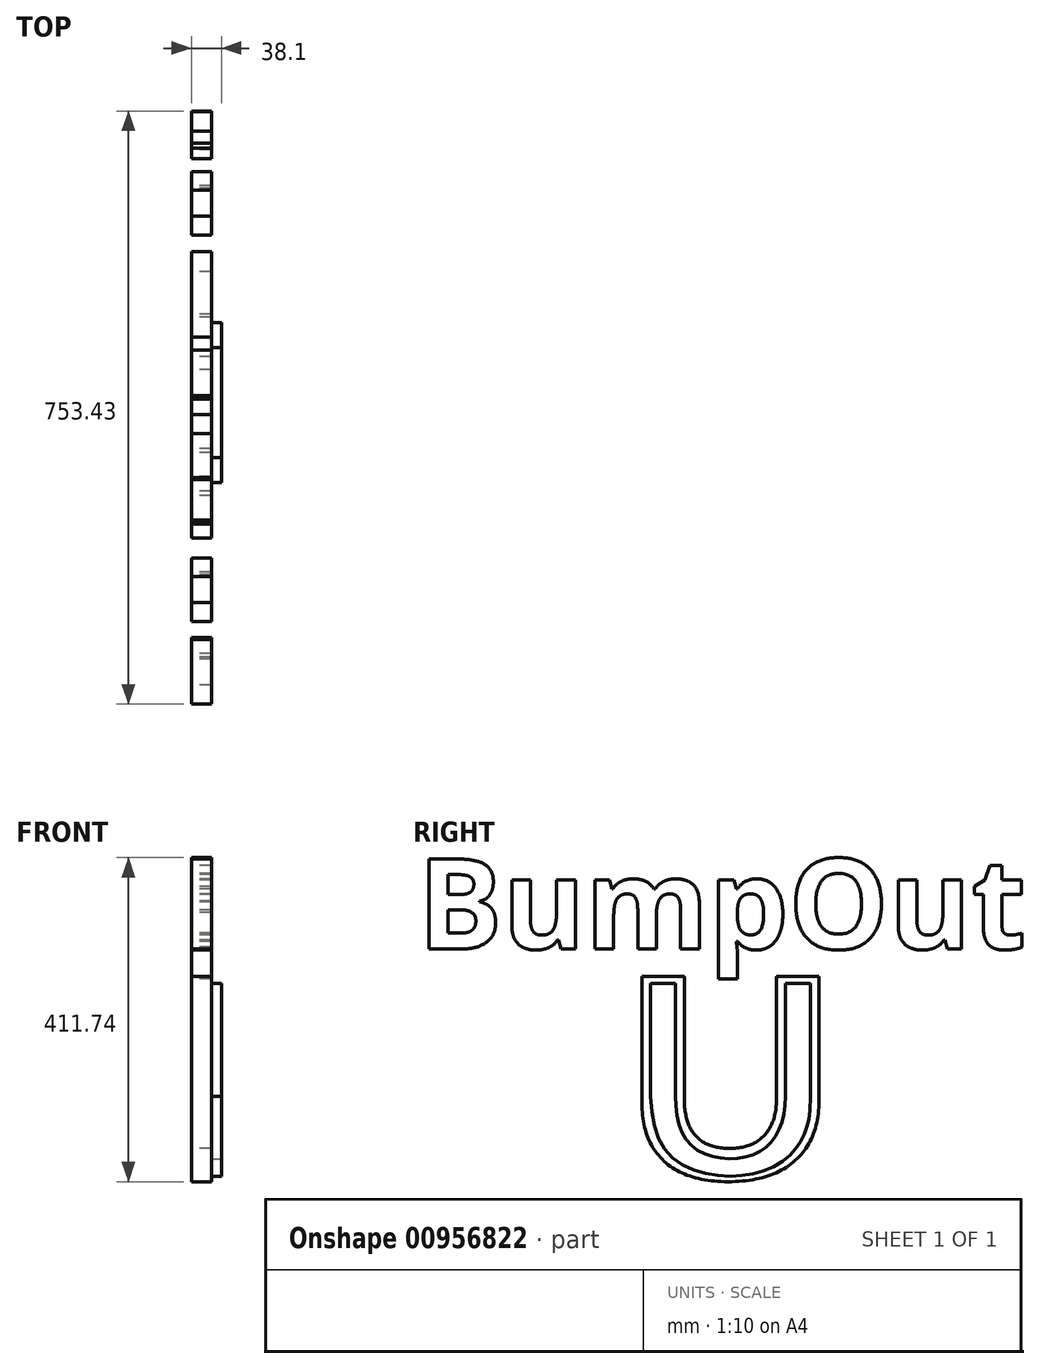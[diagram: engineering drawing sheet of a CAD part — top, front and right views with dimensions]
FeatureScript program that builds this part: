
annotation { "Feature Type Name" : "Feature", "Feature Type Description" : "" }
export const myFeature = defineFeature(function(context is Context, id is Id, definition is map)
    precondition{}
    {
        {
            var Q0;
            Q0=qCreatedBy(makeId("Right.planeOp"),FACE);
            var sketch = newSketch(context, id + "F0", { "sketchPlane" : qUnion([Q0])});
            skText(sketch, "E0", { "text": "BumpOut", "fontName": "OpenSans-Bold.ttf"});
            const initialGuessF0  = {"E0": [-0.07763, -0.0437, 1, 0, 0.1152]};
            skSetInitialGuess(sketch, initialGuessF0);
            skSolve(sketch);
        }
        {
            var Q0;
            Q0=makeQuery(id+"F0.imprint","IMPRINT",FACE,{"disambiguationData":[TD([[makeQuery(id+"F0.imprint","IMPRINT",EDGE,{"derivedFrom":sQuery(id+"F0.wireOp",EDGE,"E0.sketch_text.stroke-0")}),-1.0]])]});
            var Q1;
            Q1=makeQuery(id+"F0.imprint","IMPRINT",FACE,{"disambiguationData":[TD([[makeQuery(id+"F0.imprint","IMPRINT",EDGE,{"derivedFrom":sQuery(id+"F0.wireOp",EDGE,"E0.sketch_text.stroke-25")}),-1.0]])]});
            var Q2;
            Q2=makeQuery(id+"F0.imprint","IMPRINT",FACE,{"disambiguationData":[TD([[makeQuery(id+"F0.imprint","IMPRINT",EDGE,{"derivedFrom":sQuery(id+"F0.wireOp",EDGE,"E0.sketch_text.stroke-42")}),-1.0]])]});
            var Q3;
            Q3=makeQuery(id+"F0.imprint","IMPRINT",FACE,{"disambiguationData":[TD([[makeQuery(id+"F0.imprint","IMPRINT",EDGE,{"derivedFrom":sQuery(id+"F0.wireOp",EDGE,"E0.sketch_text.stroke-70")}),-1.0]])]});
            var Q4;
            Q4=makeQuery(id+"F0.imprint","IMPRINT",FACE,{"disambiguationData":[TD([[makeQuery(id+"F0.imprint","IMPRINT",EDGE,{"derivedFrom":sQuery(id+"F0.wireOp",EDGE,"E0.sketch_text.stroke-93")}),-1.0]])]});
            var Q5;
            Q5=makeQuery(id+"F0.imprint","IMPRINT",FACE,{"disambiguationData":[TD([[makeQuery(id+"F0.imprint","IMPRINT",EDGE,{"derivedFrom":sQuery(id+"F0.wireOp",EDGE,"E0.sketch_text.stroke-107")}),-1.0]])]});
            var Q6;
            Q6=makeQuery(id+"F0.imprint","IMPRINT",FACE,{"disambiguationData":[TD([[makeQuery(id+"F0.imprint","IMPRINT",EDGE,{"derivedFrom":sQuery(id+"F0.wireOp",EDGE,"E0.sketch_text.stroke-124")}),-1.0]])]});
            extrude(context, id + "F1", {"entities" : qUnion([Q0, Q1, Q2, Q3, Q4, Q5, Q6]), "depth" : 25.4 * mm, "offsetDistance" : 25.4 * mm});
        }
        {
            var Q0;
            Q0=qCreatedBy(makeId("Right.planeOp"),FACE);
            var sketch = newSketch(context, id + "F2", { "sketchPlane" : qUnion([Q0])});
            skText(sketch, "E1", { "text": "U", "fontName": "Arimo-Bold.ttf"});
            const initialGuessF2  = {"E1": [0.1848, -0.33573, 1, 0, 0.26936]};
            skSetInitialGuess(sketch, initialGuessF2);
            skSolve(sketch);
        }
        {
            var Q0;
            Q0=makeQuery(id+"F2.imprint","IMPRINT",FACE,{"disambiguationData":[TD([[makeQuery(id+"F2.imprint","IMPRINT",EDGE,{"derivedFrom":sQuery(id+"F2.wireOp",EDGE,"E1.sketch_text.stroke-0")}),-1.0]])]});
            extrude(context, id + "F3", {"entities" : qUnion([Q0]), "depth" : 25.4 * mm, "offsetDistance" : 25.4 * mm});
        }
        {
            var Q0;
            Q0=makeQuery(id+"F3.opExtrude","CAP_FACE",FACE,{"disambiguationData":[OSD([sQuery(id+"F2.wireOp",EDGE,"E1.sketch_text.stroke-0"),sQuery(id+"F2.wireOp",EDGE,"E1.sketch_text.stroke-1"),sQuery(id+"F2.wireOp",EDGE,"E1.sketch_text.stroke-2"),sQuery(id+"F2.wireOp",EDGE,"E1.sketch_text.stroke-3"),sQuery(id+"F2.wireOp",EDGE,"E1.sketch_text.stroke-4"),sQuery(id+"F2.wireOp",EDGE,"E1.sketch_text.stroke-5"),sQuery(id+"F2.wireOp",EDGE,"E1.sketch_text.stroke-6"),sQuery(id+"F2.wireOp",EDGE,"E1.sketch_text.stroke-7"),sQuery(id+"F2.wireOp",EDGE,"E1.sketch_text.stroke-8"),sQuery(id+"F2.wireOp",EDGE,"E1.sketch_text.stroke-9"),sQuery(id+"F2.wireOp",EDGE,"E1.sketch_text.stroke-10"),sQuery(id+"F2.wireOp",EDGE,"E1.sketch_text.stroke-11"),sQuery(id+"F2.wireOp",EDGE,"E1.sketch_text.stroke-12"),sQuery(id+"F2.wireOp",EDGE,"E1.sketch_text.stroke-13")])],"isStart":false});
            var sketch = newSketch(context, id + "F4", { "sketchPlane" : qUnion([Q0])});
            skLineSegment(sketch, "E2", {"start": v(218.32, -87.7) * mm, "end": v(250.07, -87.7) * mm});
            skLineSegment(sketch, "E3", {"start": v(250.07, -87.7) * mm, "end": v(250.07, -231.32) * mm});
            skLineSegment(sketch, "E4", {"start": v(218.32, -87.7) * mm, "end": v(218.32, -231.32) * mm});
            skLineSegment(sketch, "E5", {"start": v(389.43, -87.7) * mm, "end": v(421.18, -87.7) * mm});
            skLineSegment(sketch, "E6", {"start": v(421.18, -87.7) * mm, "end": v(421.18, -231.32) * mm});
            skLineSegment(sketch, "E7", {"start": v(389.43, -87.7) * mm, "end": v(389.43, -231.32) * mm});
            skFitSpline(sketch, "E8", {"points": [v(250.07, -231.32) * mm, v(263.62, -286.14) * mm, v(302.06, -308.47) * mm, v(349.33, -304.84) * mm, v(378.42, -279.38) * mm, v(389.43, -231.32) * mm], "startDerivative": vector(0, -279.56) * mm, "endDerivative": vector(0, 266.4) * mm});
            skFitSpline(sketch, "E9", {"points": [v(218.32, -231.32) * mm, v(232.98, -293.4) * mm, v(269.86, -323.53) * mm, v(320.76, -332.36) * mm, v(362.37, -325.43) * mm, v(392.96, -307.95) * mm, v(409.06, -287.7) * mm, v(417.9, -266.89) * mm, v(421.18, -231.32) * mm], "startDerivative": vector(14.87, -472.5) * mm, "endDerivative": vector(-3.7, 513.08) * mm});
            skSolve(sketch);
        }
        {
            var Q0;
            Q0=makeQuery(id+"F4.imprint","IMPRINT",FACE,{"disambiguationData":[TD([[makeQuery(id+"F4.imprint","IMPRINT",EDGE,{"derivedFrom":sQuery(id+"F4.wireOp",EDGE,"E2")}),-1.0]])]});
            extrude(context, id + "F5", {"entities" : qUnion([Q0]), "depth" : 12.7 * mm, "offsetDistance" : 25.4 * mm});
        }
    });
